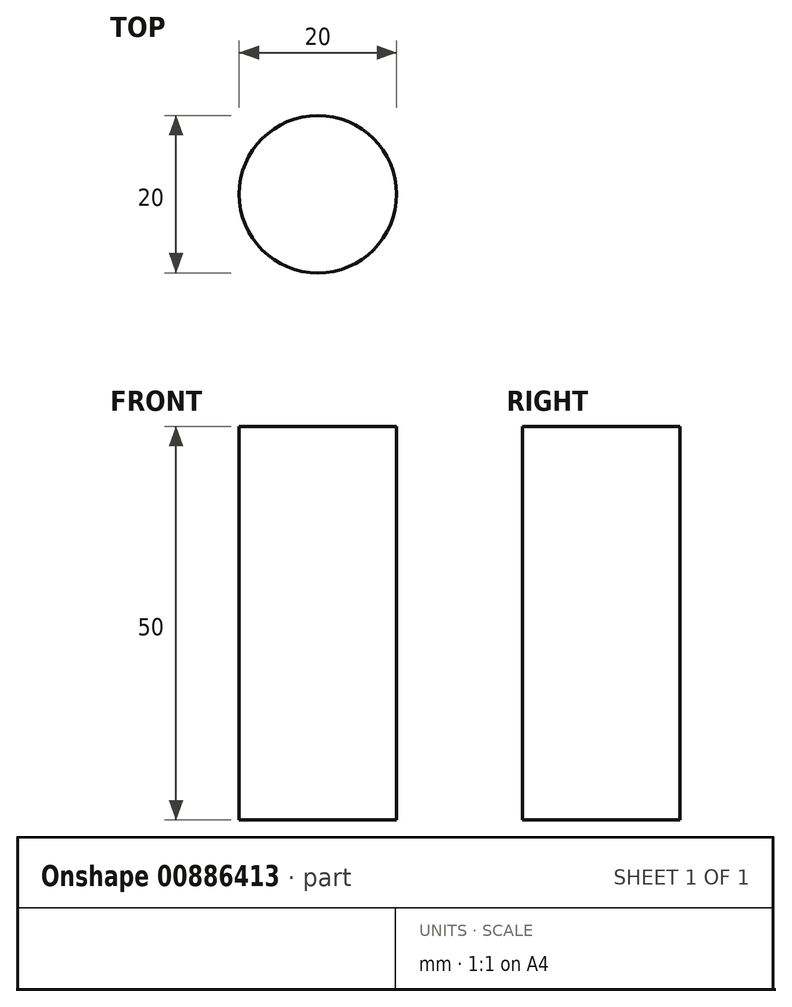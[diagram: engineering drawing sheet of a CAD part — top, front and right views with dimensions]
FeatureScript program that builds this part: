
annotation { "Feature Type Name" : "Feature", "Feature Type Description" : "" }
export const myFeature = defineFeature(function(context is Context, id is Id, definition is map)
    precondition{}
    {
        {
            var Q0;
            Q0=qCreatedBy(makeId("Top.planeOp"),FACE);
            var sketch = newSketch(context, id + "F0", { "sketchPlane" : qUnion([Q0])});
            skCircle(sketch, "E0", {"center": v(0, 0) * mm, "radius": 10 * mm});
            skSolve(sketch);
        }
        {
            var Q0;
            Q0=makeQuery(id+"F0.imprint","IMPRINT",FACE,{"disambiguationData":[TD([[makeQuery(id+"F0.imprint","IMPRINT",EDGE,{"derivedFrom":sQuery(id+"F0.wireOp",EDGE,"E0")}),1.0]])]});
            extrude(context, id + "F1", {"entities" : qUnion([Q0]), "depth" : 50 * mm, "offsetDistance" : 25 * mm});
        }
    });
